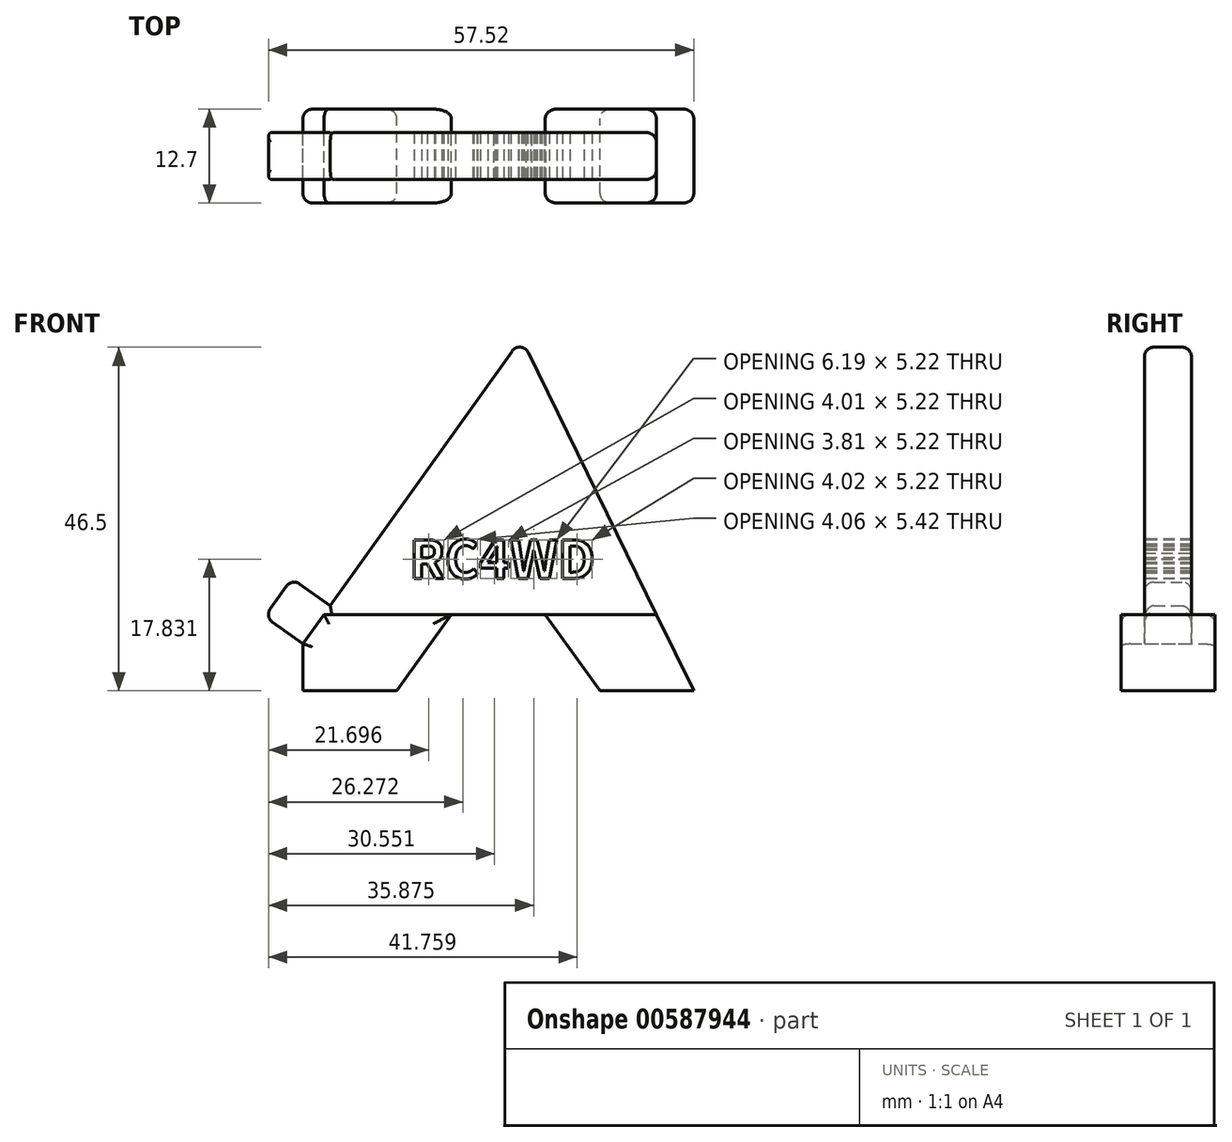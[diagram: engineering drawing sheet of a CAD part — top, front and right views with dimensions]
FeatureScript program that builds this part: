
annotation { "Feature Type Name" : "Feature", "Feature Type Description" : "" }
export const myFeature = defineFeature(function(context is Context, id is Id, definition is map)
    precondition{}
    {
        {
            var Q0;
            Q0=qCreatedBy(makeId("Front.planeOp"),FACE);
            var sketch = newSketch(context, id + "F0", { "sketchPlane" : qUnion([Q0])});
            skLineSegment(sketch, "E0", {"start": v(-3.27, 37.36) * mm, "end": v(-29.09, 1.18) * mm});
            skLineSegment(sketch, "E1", {"start": v(-29.09, 1.18) * mm, "end": v(-34.26, 4.87) * mm});
            skLineSegment(sketch, "E2", {"start": v(-34.26, 4.87) * mm, "end": v(-37.95, -0.3) * mm});
            skLineSegment(sketch, "E3", {"start": v(-37.95, -0.3) * mm, "end": v(-32.78, -3.99) * mm});
            skLineSegment(sketch, "E4", {"start": v(-32.78, -3.99) * mm, "end": v(-29.09, 1.18) * mm});
            skLineSegment(sketch, "E5", {"start": v(-32.78, -3.99) * mm, "end": v(-32.78, -10.34) * mm});
            skLineSegment(sketch, "E6", {"start": v(-32.78, -10.34) * mm, "end": v(-20.08, -10.34) * mm});
            skLineSegment(sketch, "E7", {"start": v(-20.08, -10.34) * mm, "end": v(-12.7, 0) * mm});
            skLineSegment(sketch, "E8", {"start": v(-12.7, 0) * mm, "end": v(0, 0) * mm});
            skLineSegment(sketch, "E9", {"start": v(0, 0) * mm, "end": v(7.38, -10.34) * mm});
            skLineSegment(sketch, "E10", {"start": v(7.38, -10.34) * mm, "end": v(20.08, -10.34) * mm});
            skLineSegment(sketch, "E11", {"start": v(20.08, -10.34) * mm, "end": v(-3.27, 37.36) * mm});
            skLineSegment(sketch, "E12", {"start": v(0, 0) * mm, "end": v(15.02, 0) * mm});
            skLineSegment(sketch, "E13", {"start": v(15.02, 0) * mm, "end": v(-12.7, 0) * mm});
            skLineSegment(sketch, "E14", {"start": v(-29.93, 0) * mm, "end": v(-12.7, 0) * mm});
            skSolve(sketch);
        }
        {
            var Q0;
            {var subQ4=sQuery(id+"F0.wireOp",EDGE,"E0");Q0=makeQuery(id+"F0.imprint","IMPRINT",FACE,{"disambiguationData":[TD([[makeQuery(id+"F0.imprint","IMPRINT",EDGE,{"derivedFrom":subQ4}),1.0]])]});}
            var Q1;
            {var subQ3=sQuery(id+"F0.wireOp",EDGE,"E1");Q1=makeQuery(id+"F0.imprint","IMPRINT",FACE,{"disambiguationData":[TD([[makeQuery(id+"F0.imprint","IMPRINT",EDGE,{"derivedFrom":subQ3}),1.0]])]});}
            extrude(context, id + "F1", {"entities" : qUnion([Q0, Q1]), "endBound" : BoundingType.SYMMETRIC, "depth" : 6.35 * mm, "offsetDistance" : 25.4 * mm});
        }
        {
            var Q0;
            {var subQ0=sQuery(id+"F0.wireOp",EDGE,"E5");Q0=makeQuery(id+"F0.imprint","IMPRINT",FACE,{"disambiguationData":[TD([[makeQuery(id+"F0.imprint","IMPRINT",EDGE,{"derivedFrom":subQ0}),1.0]])]});}
            var Q1;
            {var subQ0=sQuery(id+"F0.wireOp",EDGE,"E9");Q1=makeQuery(id+"F0.imprint","IMPRINT",FACE,{"disambiguationData":[TD([[makeQuery(id+"F0.imprint","IMPRINT",EDGE,{"derivedFrom":subQ0}),1.0]])]});}
            extrude(context, id + "F2", {"entities" : qUnion([Q0, Q1]), "endBound" : BoundingType.SYMMETRIC, "depth" : 12.7 * mm, "offsetDistance" : 25.4 * mm});
        }
        {
            var Q0;
            Q0=qCreatedBy(makeId("Front.planeOp"),FACE);
            var sketch = newSketch(context, id + "F3", { "sketchPlane" : qUnion([Q0])});
            skText(sketch, "E15", { "text": "RC4WD", "fontName": "NotoSansCJKkr-Bold.otf"});
            const initialGuessF3  = {"E15": [-0.01839, 0.00488, 1, 0, 0.00508]};
            skSetInitialGuess(sketch, initialGuessF3);
            skSolve(sketch);
        }
        {
            var Q0;
            Q0 = qSketchRegion(id + "F3", true);
            extrude(context, id + "F4", {"entities" : qUnion([Q0]), "operationType" : NewBodyOperationType.REMOVE, "endBound" : BoundingType.SYMMETRIC, "oppositeDirection" : true, "depth" : 25.4 * mm, "offsetDistance" : 25.4 * mm});
        }
        {
            var Q0;
            Q0=makeQuery(id+"F1.opExtrude","CAP_EDGE",EDGE,{"disambiguationData":[OSD([sQuery(id+"F0.wireOp",EDGE,"E0")])],"isStart":false});
            var Q1;
            Q1=makeQuery(id+"F1.opExtrude","CAP_EDGE",EDGE,{"disambiguationData":[OSD([sQuery(id+"F0.wireOp",EDGE,"E11")])],"isStart":false});
            var Q2;
            Q2=makeQuery(id+"F1.opExtrude","CAP_EDGE",EDGE,{"disambiguationData":[OSD([sQuery(id+"F0.wireOp",EDGE,"E11")])],"isStart":true});
            var Q3;
            Q3=makeQuery(id+"F1.opExtrude","CAP_EDGE",EDGE,{"disambiguationData":[OSD([sQuery(id+"F0.wireOp",EDGE,"E0")])],"isStart":true});
            var Q4;
            Q4=makeQuery(id+"F1.opExtrude","SWEPT_EDGE",EDGE,{"disambiguationData":[OSD([sQuery(id+"F0.wireOp",EDGE,"E0"),sQuery(id+"F0.wireOp",EDGE,"E11")])]});
            var Q5;
            Q5=makeQuery(id+"F1.opExtrude","SWEPT_EDGE",EDGE,{"disambiguationData":[OSD([sQuery(id+"F0.wireOp",EDGE,"E1"),sQuery(id+"F0.wireOp",EDGE,"E2")])]});
            var Q6;
            Q6=makeQuery(id+"F1.opExtrude","SWEPT_FACE",FACE,{"disambiguationData":[OSD([sQuery(id+"F0.wireOp",EDGE,"E2")])]});
            var Q7;
            Q7=makeQuery(id+"F1.opExtrude","CAP_EDGE",EDGE,{"disambiguationData":[OSD([sQuery(id+"F0.wireOp",EDGE,"E2")])],"isStart":false});
            var Q8;
            Q8=makeQuery(id+"F1.opExtrude","CAP_EDGE",EDGE,{"disambiguationData":[OSD([sQuery(id+"F0.wireOp",EDGE,"E2")])],"isStart":true});
            var Q9;
            Q9=makeQuery(id+"F1.opExtrude","CAP_EDGE",EDGE,{"disambiguationData":[OSD([sQuery(id+"F0.wireOp",EDGE,"E1")])],"isStart":false});
            var Q10;
            Q10=makeQuery(id+"F1.opExtrude","CAP_EDGE",EDGE,{"disambiguationData":[OSD([sQuery(id+"F0.wireOp",EDGE,"E1")])],"isStart":true});
            fillet(context, id + "F5", {"entities" : qUnion([Q0, Q1, Q2, Q3, Q4, Q5, Q6, Q7, Q8, Q9, Q10]), "radius" : 1.27 * mm, "tangentPropagation" : true, "allowEdgeOverflow" : false});
        }
        {
            var Q0;
            Q0=makeQuery(id+"F2.opExtrude","CAP_EDGE",EDGE,{"disambiguationData":[OSD([sQuery(id+"F0.wireOp",EDGE,"E11")])],"isStart":true});
            var Q1;
            Q1=makeQuery(id+"F2.opExtrude","CAP_EDGE",EDGE,{"disambiguationData":[OSD([sQuery(id+"F0.wireOp",EDGE,"E13")])],"isStart":true});
            var Q2;
            Q2=makeQuery(id+"F2.opExtrude","CAP_EDGE",EDGE,{"disambiguationData":[OSD([sQuery(id+"F0.wireOp",EDGE,"E14")])],"isStart":true});
            var Q3;
            Q3=makeQuery(id+"F2.opExtrude","CAP_EDGE",EDGE,{"disambiguationData":[OSD([sQuery(id+"F0.wireOp",EDGE,"E5")])],"isStart":true});
            var Q4;
            Q4=makeQuery(id+"F2.opExtrude","CAP_EDGE",EDGE,{"disambiguationData":[OSD([sQuery(id+"F0.wireOp",EDGE,"E7")])],"isStart":true});
            var Q5;
            Q5=makeQuery(id+"F2.opExtrude","CAP_EDGE",EDGE,{"disambiguationData":[OSD([sQuery(id+"F0.wireOp",EDGE,"E9")])],"isStart":true});
            var Q6;
            Q6=makeQuery(id+"F2.opExtrude","CAP_EDGE",EDGE,{"disambiguationData":[OSD([sQuery(id+"F0.wireOp",EDGE,"E11")])],"isStart":false});
            var Q7;
            Q7=makeQuery(id+"F2.opExtrude","CAP_EDGE",EDGE,{"disambiguationData":[OSD([sQuery(id+"F0.wireOp",EDGE,"E13")])],"isStart":false});
            var Q8;
            Q8=makeQuery(id+"F2.opExtrude","CAP_EDGE",EDGE,{"disambiguationData":[OSD([sQuery(id+"F0.wireOp",EDGE,"E9")])],"isStart":false});
            var Q9;
            Q9=makeQuery(id+"F2.opExtrude","CAP_EDGE",EDGE,{"disambiguationData":[OSD([sQuery(id+"F0.wireOp",EDGE,"E7")])],"isStart":false});
            var Q10;
            Q10=makeQuery(id+"F2.opExtrude","CAP_EDGE",EDGE,{"disambiguationData":[OSD([sQuery(id+"F0.wireOp",EDGE,"E14")])],"isStart":false});
            var Q11;
            Q11=makeQuery(id+"F2.opExtrude","CAP_EDGE",EDGE,{"disambiguationData":[OSD([sQuery(id+"F0.wireOp",EDGE,"E4")])],"isStart":false});
            var Q12;
            Q12=makeQuery(id+"F2.opExtrude","CAP_EDGE",EDGE,{"disambiguationData":[OSD([sQuery(id+"F0.wireOp",EDGE,"E5")])],"isStart":false});
            var Q13;
            Q13=makeQuery(id+"F2.opExtrude","CAP_EDGE",EDGE,{"disambiguationData":[OSD([sQuery(id+"F0.wireOp",EDGE,"E4")])],"isStart":true});
            fillet(context, id + "F6", {"entities" : qUnion([Q0, Q1, Q2, Q3, Q4, Q5, Q6, Q7, Q8, Q9, Q10, Q11, Q12, Q13]), "radius" : 1.27 * mm, "tangentPropagation" : true, "allowEdgeOverflow" : false});
        }
    });
